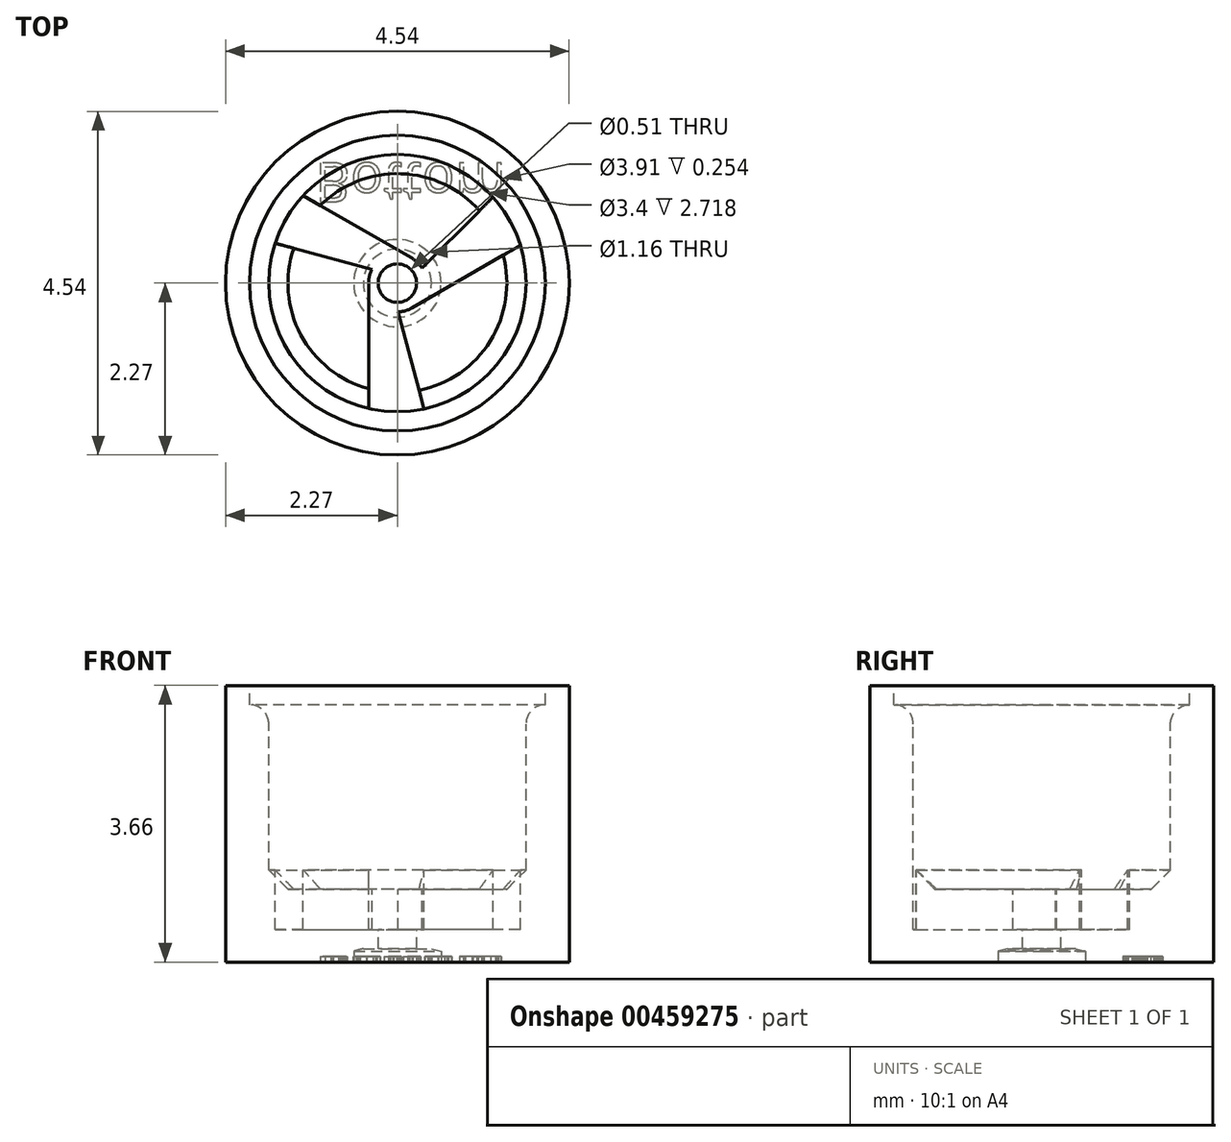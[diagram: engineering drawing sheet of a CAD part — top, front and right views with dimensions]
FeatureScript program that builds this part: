
annotation { "Feature Type Name" : "Feature", "Feature Type Description" : "" }
export const myFeature = defineFeature(function(context is Context, id is Id, definition is map)
    precondition{}
    {
        {
            var Q0;
            Q0=qCreatedBy(makeId("Top.planeOp"),FACE);
            var sketch = newSketch(context, id + "F0", { "sketchPlane" : qUnion([Q0])});
            skCircle(sketch, "E0", {"center": v(0, 0) * mm, "radius": 2.27 * mm});
            skSolve(sketch);
        }
        {
            var Q0;
            Q0=qSketchRegion(id+"F0",true);
            extrude(context, id + "F1", {"entities" : qUnion([Q0]), "depth" : 3.66 * mm});
        }
        {
            var Q0;
            Q0=makeQuery(id+"F1.opExtrude","CAP_FACE",FACE,{"disambiguationData":[OSD([sQuery(id+"F0.wireOp",EDGE,"E0")])],"isStart":false});
            var sketch = newSketch(context, id + "F2", { "sketchPlane" : qUnion([Q0])});
            skCircle(sketch, "E1", {"center": v(0, 0) * mm, "radius": 1.96 * mm});
            skSolve(sketch);
        }
        {
            var Q0;
            Q0=makeQuery(id+"F2.imprint","IMPRINT",FACE,{"disambiguationData":[TD([[makeQuery(id+"F2.imprint","IMPRINT",EDGE,{"derivedFrom":sQuery(id+"F2.wireOp",EDGE,"E1")}),1.0]])]});
            extrude(context, id + "F3", {"entities" : qUnion([Q0]), "operationType" : NewBodyOperationType.REMOVE, "oppositeDirection" : true, "depth" : 0.25 * mm});
        }
        {
            var Q0;
            Q0=makeQuery(id+"F3.boolean.opBoolean","COPY",FACE,{"derivedFrom":makeQuery(id+"F3.opExtrude","CAP_FACE",FACE,{"disambiguationData":[OSD([sQuery(id+"F2.wireOp",EDGE,"E1")])],"isStart":false})});
            var sketch = newSketch(context, id + "F4", { "sketchPlane" : qUnion([Q0])});
            skCircle(sketch, "E2", {"center": v(0, 0) * mm, "radius": 1.7 * mm});
            skSolve(sketch);
        }
        {
            var Q0;
            Q0=makeQuery(id+"F4.imprint","IMPRINT",FACE,{"disambiguationData":[TD([[makeQuery(id+"F4.imprint","IMPRINT",EDGE,{"derivedFrom":sQuery(id+"F4.wireOp",EDGE,"E2")}),1.0]])]});
            extrude(context, id + "F5", {"entities" : qUnion([Q0]), "operationType" : NewBodyOperationType.REMOVE, "oppositeDirection" : true, "depth" : 2.44 * mm});
        }
        {
            var Q0;
            Q0=makeQuery(id+"F5.boolean.opBoolean","COPY",EDGE,{"derivedFrom":makeQuery(id+"F5.opExtrude","CAP_EDGE",EDGE,{"disambiguationData":[OSD([sQuery(id+"F4.wireOp",EDGE,"E2")])],"isStart":false})});
            chamfer(context, id + "F6", {"entities" : qUnion([Q0]), "chamferType" : ChamferType.OFFSET_ANGLE, "width" : 0.25 * mm, "oppositeDirection" : false, "angle" : 45 * degree, "tangentPropagation" : true});
        }
        {
            var Q0;
            Q0=makeQuery(id+"F5.boolean.opBoolean","COPY",FACE,{"derivedFrom":makeQuery(id+"F5.opExtrude","CAP_FACE",FACE,{"disambiguationData":[OSD([sQuery(id+"F4.wireOp",EDGE,"E2")])],"isStart":false})});
            var sketch = newSketch(context, id + "F7", { "sketchPlane" : qUnion([Q0])});
            skCircle(sketch, "E3", {"center": v(0, 0) * mm, "radius": 0.38 * mm});
            skSolve(sketch);
        }
        {
            var Q0;
            Q0=makeQuery(id+"F7.imprint","IMPRINT",FACE,{"disambiguationData":[TD([[makeQuery(id+"F7.imprint","IMPRINT",EDGE,{"derivedFrom":sQuery(id+"F7.wireOp",EDGE,"E3")}),1.0]])]});
            extrude(context, id + "F8", {"entities" : qUnion([Q0]), "operationType" : NewBodyOperationType.REMOVE, "oppositeDirection" : true, "depth" : 0.53 * mm});
        }
        {
            var Q0;
            Q0=makeQuery(id+"F8.boolean.opBoolean","COPY",FACE,{"derivedFrom":makeQuery(id+"F8.opExtrude","CAP_FACE",FACE,{"disambiguationData":[OSD([sQuery(id+"F7.wireOp",EDGE,"E3")])],"isStart":false})});
            var sketch = newSketch(context, id + "F9", { "sketchPlane" : qUnion([Q0])});
            skCircle(sketch, "E4", {"center": v(0, 0) * mm, "radius": 0.25 * mm});
            skSolve(sketch);
        }
        {
            var Q0;
            Q0=makeQuery(id+"F9.imprint","IMPRINT",FACE,{"disambiguationData":[TD([[makeQuery(id+"F9.imprint","IMPRINT",EDGE,{"derivedFrom":sQuery(id+"F9.wireOp",EDGE,"E4")}),1.0]])]});
            extrude(context, id + "F10", {"entities" : qUnion([Q0]), "operationType" : NewBodyOperationType.REMOVE, "oppositeDirection" : true, "depth" : 25.4 * mm});
        }
        {
            var Q0;
            Q0=makeQuery(id+"F1.opExtrude","CAP_FACE",FACE,{"disambiguationData":[OSD([sQuery(id+"F0.wireOp",EDGE,"E0")])],"isStart":true});
            var sketch = newSketch(context, id + "F11", { "sketchPlane" : qUnion([Q0])});
            skCircle(sketch, "E5", {"center": v(0, 0) * mm, "radius": 0.58 * mm});
            skSolve(sketch);
        }
        {
            var Q0;
            Q0=makeQuery(id+"F11.imprint","IMPRINT",FACE,{"disambiguationData":[TD([[makeQuery(id+"F11.imprint","IMPRINT",EDGE,{"derivedFrom":sQuery(id+"F11.wireOp",EDGE,"E5")}),1.0]])]});
            extrude(context, id + "F12", {"entities" : qUnion([Q0]), "operationType" : NewBodyOperationType.REMOVE, "oppositeDirection" : true, "depth" : 0.18 * mm});
        }
        {
            var Q0;
            Q0=makeQuery(id+"F12.boolean.opBoolean","COPY",EDGE,{"derivedFrom":makeQuery(id+"F12.opExtrude","CAP_EDGE",EDGE,{"disambiguationData":[OSD([sQuery(id+"F11.wireOp",EDGE,"E5")])],"isStart":false})});
            chamfer(context, id + "F13", {"entities" : qUnion([Q0]), "chamferType" : ChamferType.OFFSET_ANGLE, "width" : 0.13 * mm, "oppositeDirection" : false, "angle" : 15 * degree, "tangentPropagation" : true});
        }
        {
            var Q0;
            Q0=makeQuery(id+"F5.boolean.opBoolean","COPY",FACE,{"derivedFrom":makeQuery(id+"F5.opExtrude","CAP_FACE",FACE,{"disambiguationData":[OSD([sQuery(id+"F4.wireOp",EDGE,"E2")])],"isStart":false})});
            var sketch = newSketch(context, id + "F14", { "sketchPlane" : qUnion([Q0])});
            skArc(sketch, "E6.0", {"start": v(0.2, 0.33) * mm, "mid": v(-0.1, 0.37) * mm, "end": v(-0.33, 0.18) * mm});
            skArc(sketch, "E7.0", {"start": v(-1.25, 1.16) * mm, "mid": v(-1.47, 0.86) * mm, "end": v(-1.62, 0.53) * mm});
            skLineSegment(sketch, "E8", {"start": v(0.2, 0.33) * mm, "end": v(-1.25, 1.16) * mm});
            skLineSegment(sketch, "E9", {"start": v(-0.33, 0.18) * mm, "end": v(-1.62, 0.53) * mm});
            skLineSegment(sketch, "E10.1.0", {"start": v(-0.38, 0) * mm, "end": v(-0.38, -1.66) * mm});
            skArc(sketch, "E10.1.1", {"start": v(-0.38, 0) * mm, "mid": v(-0.27, -0.27) * mm, "end": v(0, -0.38) * mm});
            skLineSegment(sketch, "E10.1.2", {"start": v(0, -0.38) * mm, "end": v(0.35, -1.66) * mm});
            skArc(sketch, "E10.1.3", {"start": v(-0.38, -1.66) * mm, "mid": v(-0.01, -1.7) * mm, "end": v(0.35, -1.66) * mm});
            skLineSegment(sketch, "E10.2.0", {"start": v(0.2, -0.33) * mm, "end": v(1.63, 0.5) * mm});
            skArc(sketch, "E10.2.1", {"start": v(0.2, -0.33) * mm, "mid": v(0.37, -0.1) * mm, "end": v(0.33, 0.2) * mm});
            skLineSegment(sketch, "E10.2.2", {"start": v(0.33, 0.2) * mm, "end": v(1.27, 1.14) * mm});
            skArc(sketch, "E10.2.3", {"start": v(1.63, 0.5) * mm, "mid": v(1.48, 0.84) * mm, "end": v(1.27, 1.14) * mm});
            skSolve(sketch);
        }
        {
            var Q0;
            Q0=qSketchRegion(id+"F14",true);
            var Q1;
            Q1=makeQuery(id+"F8.boolean.opBoolean","COPY",FACE,{"derivedFrom":makeQuery(id+"F8.opExtrude","CAP_FACE",FACE,{"disambiguationData":[OSD([sQuery(id+"F7.wireOp",EDGE,"E3")])],"isStart":false})});
            extrude(context, id + "F15", {"entities" : qUnion([Q0]), "operationType" : NewBodyOperationType.REMOVE, "endBound" : BoundingType.UP_TO_SURFACE, "oppositeDirection" : true, "endBoundEntityFace" : qUnion([Q1]), "depth" : 0.33 * mm});
        }
        {
            var Q0;
            Q0=qSketchRegion(id+"F14",true);
            extrude(context, id + "F16", {"entities" : qUnion([Q0]), "operationType" : NewBodyOperationType.REMOVE, "depth" : 25.4 * mm});
        }
        {
            var Q0;
            Q0=makeQuery(id+"F16.boolean.opBoolean","INTERSECT",EDGE,{"derivedFrom":[makeQuery(id+"F16.opExtrude","SWEPT_FACE",FACE,{"disambiguationData":[OSD([sQuery(id+"F14.wireOp",EDGE,"E7.0")])]}),makeQuery(id+"F16.opExtrude","SWEPT_FACE",FACE,{"disambiguationData":[OSD([sQuery(id+"F14.wireOp",EDGE,"E10.1.3")])]}),makeQuery(id+"F16.opExtrude","SWEPT_FACE",FACE,{"disambiguationData":[OSD([sQuery(id+"F14.wireOp",EDGE,"E10.2.3")])]})]});
            fillet(context, id + "F17", {"entities" : qUnion([Q0]), "radius" : 0.25 * mm, "tangentPropagation" : true, "allowEdgeOverflow" : false});
        }
        {
            var Q0;
            Q0=makeQuery(id+"F1.opExtrude","CAP_FACE",FACE,{"disambiguationData":[OSD([sQuery(id+"F0.wireOp",EDGE,"E0")])],"isStart":true});
            var sketch = newSketch(context, id + "F18", { "sketchPlane" : qUnion([Q0])});
            skText(sketch, "E11", { "text": "Bottom", "fontName": "OpenSans-Regular.ttf"});
            const initialGuessF18  = {"E11": [-0.00109, -0.00159, 1, 0, 0.00052]};
            skSetInitialGuess(sketch, initialGuessF18);
            skSolve(sketch);
        }
        {
            var Q0;
            Q0=qSketchRegion(id+"F18",true);
            extrude(context, id + "F19", {"entities" : qUnion([Q0]), "operationType" : NewBodyOperationType.REMOVE, "oppositeDirection" : true, "depth" : 0.08 * mm});
        }
    });
